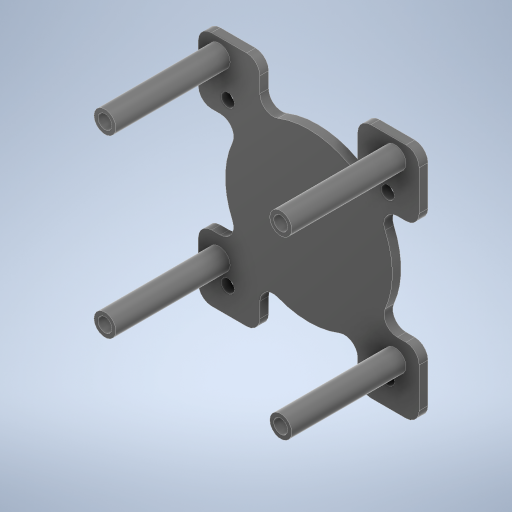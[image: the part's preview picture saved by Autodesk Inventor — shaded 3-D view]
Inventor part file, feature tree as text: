
AUTODESK INVENTOR PART (.ipt)
format: ipt  version: 2023.1 (Build 271208000, 208)  size: 362,496 bytes
history: native  units: in
note: dims shown in document units (in); Inventor stores cm internally (conversion verified against a paired STEP export)
features: reference x13, other x6, extrude x2, fillet x2, sketch x2, plane x1
ambient origin geometry x8: Origin, YZ Plane, XZ Plane, XY Plane, X Axis, Y Axis, Z Axis, Center Point
bodies: Solid1 (feature_tree)
feature tree (26):
  plane  "Work Plane1"
  extrude  "Extrusion1"  Depth=1.9783in
  fillet  "Fillet1"  Radius=2.1181in
  fillet  "Fillet2"  Radius=1.0591in
  extrude  "Extrusion2"  Depth=0.1181in
  sketch  "Sketch1"  dims[d0=0.0787in d1=0.0in d10=1.9783in d11=2.1181in d12=0.9892in d13=1.0591in]
  reference  "Reference1"
  reference  "Reference2"
  reference  "Reference3"
  reference  "Reference4"
  reference  "Reference5"
  reference  "Reference6"
  reference  "Reference7"
  reference  "Reference8"
  reference  "Reference9"
  sketch  "Sketch2"  dims[d14=1.4961in d15=0.1181in d16=0.1181in d17=0.1969in d18=0.1969in d19=0.1969in d20=0.1969in d21=1.0236in d22=0.0in]
  reference  "Reference10"
  reference  "Reference11"
  reference  "Reference12"
  reference  "Reference13"
  other  "Assembly2"
  other  "Assembly - Fixed:1"
  other  "BaseParal:1"
  other  "BTS7960 43A HIGH POWER H BRIDGE MODULE:1"
  other  "PCB, BTS7960 43A HIGH POWER H BRIDGE MODULE_1"
  other  "HEATSINK, BTS7960 43A HIGH POWER H BRIDGE MODULE_2"
